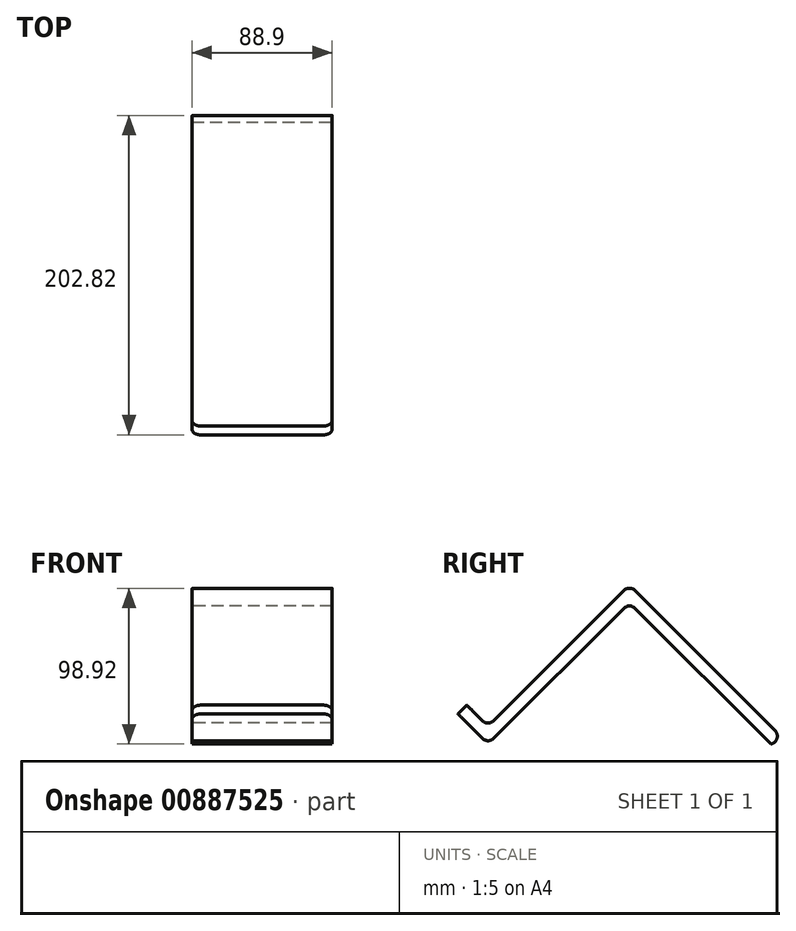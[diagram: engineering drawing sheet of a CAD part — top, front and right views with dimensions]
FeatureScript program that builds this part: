
annotation { "Feature Type Name" : "Feature", "Feature Type Description" : "" }
export const myFeature = defineFeature(function(context is Context, id is Id, definition is map)
    precondition{}
    {
        {
            var Q0;
            Q0=qCreatedBy(makeId("Right.planeOp"),FACE);
            var sketch = newSketch(context, id + "F0", { "sketchPlane" : qUnion([Q0])});
            skLineSegment(sketch, "E0", {"start": v(0, 0) * mm, "end": v(-101.03, 101.03) * mm});
            skLineSegment(sketch, "E1", {"start": v(-101.03, 101.03) * mm, "end": v(-190.83, 11.23) * mm});
            skLineSegment(sketch, "E2", {"start": v(-190.83, 11.23) * mm, "end": v(-204.3, 24.7) * mm});
            skLineSegment(sketch, "E3", {"start": v(0, 0) * mm, "end": v(-209.91, 0) * mm, "construction": true});
            skLineSegment(sketch, "E4", {"start": v(-101.03, 101.03) * mm, "end": v(-101.03, 0) * mm, "construction": true});
            skLineSegment(sketch, "E5", {"start": v(-190.83, 0) * mm, "end": v(-190.83, 11.23) * mm, "construction": true});
            skLineSegment(sketch, "E6", {"start": v(-190.83, 0) * mm, "end": v(-101.03, 89.8) * mm});
            skLineSegment(sketch, "E7", {"start": v(-101.03, 89.8) * mm, "end": v(-11.23, 0) * mm});
            skLineSegment(sketch, "E8", {"start": v(-190.83, 0) * mm, "end": v(-209.91, 19.08) * mm});
            skLineSegment(sketch, "E9", {"start": v(-204.3, 24.7) * mm, "end": v(-209.91, 19.08) * mm});
            skLineSegment(sketch, "E10", {"start": v(-209.91, 0) * mm, "end": v(-209.91, 19.08) * mm, "construction": true});
            skLineSegment(sketch, "E11", {"start": v(-11.23, 0) * mm, "end": v(0, 0) * mm});
            skSolve(sketch);
        }
        {
            var Q0;
            Q0=makeQuery(id+"F0.imprint","IMPRINT",FACE,{"disambiguationData":[TD([[makeQuery(id+"F0.imprint","IMPRINT",EDGE,{"derivedFrom":sQuery(id+"F0.wireOp",EDGE,"E0")}),1.0]])]});
            extrude(context, id + "F1", {"entities" : qUnion([Q0]), "oppositeDirection" : true, "depth" : 88.9 * mm, "offsetDistance" : 25.4 * mm});
        }
        {
            var Q0;
            Q0=makeQuery(id+"F1.opExtrude","SWEPT_EDGE",EDGE,{"disambiguationData":[OSD([sQuery(id+"F0.wireOp",EDGE,"E1"),sQuery(id+"F0.wireOp",EDGE,"E2")])]});
            var Q1;
            Q1=makeQuery(id+"F1.opExtrude","SWEPT_EDGE",EDGE,{"disambiguationData":[OSD([sQuery(id+"F0.wireOp",EDGE,"E6"),sQuery(id+"F0.wireOp",EDGE,"E8")])]});
            var Q2;
            Q2=makeQuery(id+"F1.opExtrude","SWEPT_EDGE",EDGE,{"disambiguationData":[OSD([sQuery(id+"F0.wireOp",EDGE,"E0"),sQuery(id+"F0.wireOp",EDGE,"E1")])]});
            var Q3;
            Q3=makeQuery(id+"F1.opExtrude","SWEPT_EDGE",EDGE,{"disambiguationData":[OSD([sQuery(id+"F0.wireOp",EDGE,"E6"),sQuery(id+"F0.wireOp",EDGE,"E7")])]});
            var Q4;
            Q4=makeQuery(id+"F1.opExtrude","SWEPT_EDGE",EDGE,{"disambiguationData":[OSD([sQuery(id+"F0.wireOp",EDGE,"E0"),sQuery(id+"F0.wireOp",EDGE,"E11")])]});
            var Q5;
            Q5=makeQuery(id+"F1.opExtrude","CAP_EDGE",EDGE,{"disambiguationData":[OSD([sQuery(id+"F0.wireOp",EDGE,"E9")])],"isStart":true});
            var Q6;
            Q6=makeQuery(id+"F1.opExtrude","CAP_EDGE",EDGE,{"disambiguationData":[OSD([sQuery(id+"F0.wireOp",EDGE,"E9")])],"isStart":false});
            fillet(context, id + "F2", {"entities" : qUnion([Q0, Q1, Q2, Q3, Q4, Q5, Q6]), "radius" : 5.08 * mm, "tangentPropagation" : true, "allowEdgeOverflow" : false});
        }
    });
